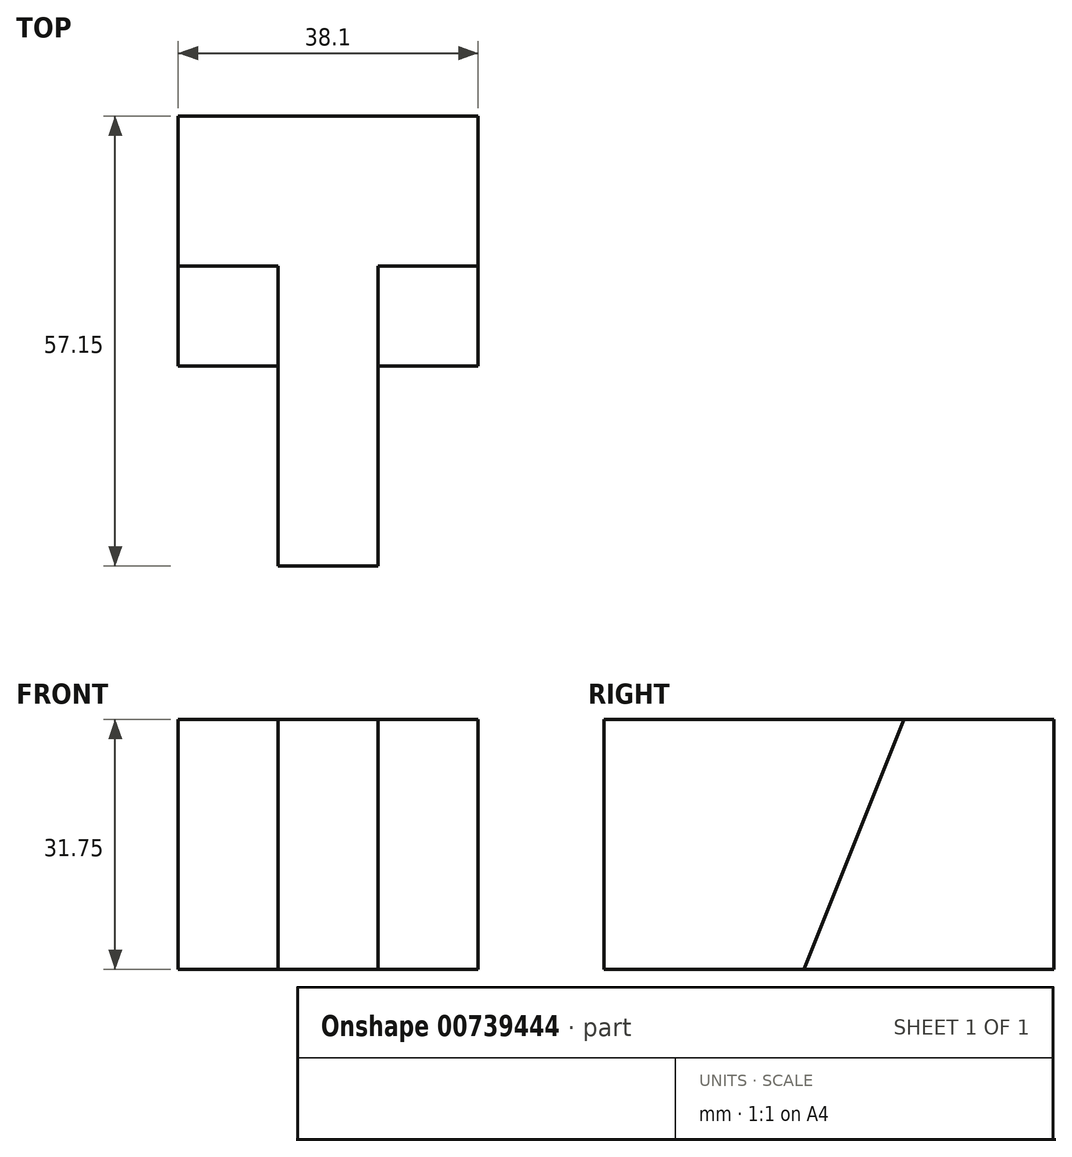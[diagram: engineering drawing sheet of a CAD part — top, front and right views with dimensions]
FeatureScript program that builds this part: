
annotation { "Feature Type Name" : "Feature", "Feature Type Description" : "" }
export const myFeature = defineFeature(function(context is Context, id is Id, definition is map)
    precondition{}
    {
        {
            var Q0;
            Q0=qCreatedBy(makeId("Top.planeOp"),FACE);
            var sketch = newSketch(context, id + "F0", { "sketchPlane" : qUnion([Q0])});
            skLineSegment(sketch, "E0", {"start": v(0, 0) * mm, "end": v(0, 25.4) * mm});
            skLineSegment(sketch, "E1", {"start": v(0, 25.4) * mm, "end": v(-12.7, 25.4) * mm});
            skLineSegment(sketch, "E2", {"start": v(-12.7, 25.4) * mm, "end": v(-12.7, 57.15) * mm});
            skLineSegment(sketch, "E3", {"start": v(-12.7, 57.15) * mm, "end": v(25.4, 57.15) * mm});
            skLineSegment(sketch, "E4", {"start": v(25.4, 57.15) * mm, "end": v(25.4, 25.4) * mm});
            skLineSegment(sketch, "E5", {"start": v(25.4, 25.4) * mm, "end": v(12.7, 25.4) * mm});
            skLineSegment(sketch, "E6", {"start": v(12.7, 25.4) * mm, "end": v(12.7, 0) * mm});
            skLineSegment(sketch, "E7", {"start": v(12.7, 0) * mm, "end": v(0, 0) * mm});
            skSolve(sketch);
        }
        {
            var Q0;
            Q0=makeQuery(id+"F0.imprint","IMPRINT",FACE,{"disambiguationData":[TD([[makeQuery(id+"F0.imprint","IMPRINT",EDGE,{"derivedFrom":sQuery(id+"F0.wireOp",EDGE,"E0")}),-1.0]])]});
            extrude(context, id + "F1", {"entities" : qUnion([Q0]), "depth" : 31.75 * mm, "offsetDistance" : 25.4 * mm});
        }
        {
            var Q0;
            Q0=makeQuery(id+"F1.opExtrude","SWEPT_FACE",FACE,{"disambiguationData":[OSD([sQuery(id+"F0.wireOp",EDGE,"E2")])]});
            var sketch = newSketch(context, id + "F2", { "sketchPlane" : qUnion([Q0])});
            skLineSegment(sketch, "E8", {"start": v(-25.4, 0) * mm, "end": v(-38.1, 31.75) * mm});
            skLineSegment(sketch, "E9", {"start": v(-38.1, 31.75) * mm, "end": v(-25.4, 31.75) * mm});
            skLineSegment(sketch, "E10", {"start": v(-25.4, 31.75) * mm, "end": v(-25.4, 0) * mm});
            skSolve(sketch);
        }
        {
            var Q0;
            Q0=makeQuery(id+"F2.imprint","IMPRINT",FACE,{"disambiguationData":[TD([[makeQuery(id+"F2.imprint","IMPRINT",EDGE,{"derivedFrom":sQuery(id+"F2.wireOp",EDGE,"E8")}),-1.0]])]});
            extrude(context, id + "F3", {"entities" : qUnion([Q0]), "operationType" : NewBodyOperationType.REMOVE, "oppositeDirection" : true, "depth" : 12.7 * mm, "offsetDistance" : 25.4 * mm});
        }
        {
            var Q0;
            Q0=makeQuery(id+"F1.opExtrude","SWEPT_FACE",FACE,{"disambiguationData":[OSD([sQuery(id+"F0.wireOp",EDGE,"E4")])]});
            var sketch = newSketch(context, id + "F4", { "sketchPlane" : qUnion([Q0])});
            skLineSegment(sketch, "E11", {"start": v(38.1, 31.75) * mm, "end": v(25.4, 0) * mm});
            skLineSegment(sketch, "E12", {"start": v(25.4, 0) * mm, "end": v(25.4, 31.75) * mm});
            skLineSegment(sketch, "E13", {"start": v(25.4, 31.75) * mm, "end": v(38.1, 31.75) * mm});
            skSolve(sketch);
        }
        {
            var Q0;
            Q0=makeQuery(id+"F4.imprint","IMPRINT",FACE,{"disambiguationData":[TD([[makeQuery(id+"F4.imprint","IMPRINT",EDGE,{"derivedFrom":sQuery(id+"F4.wireOp",EDGE,"E11")}),-1.0]])]});
            extrude(context, id + "F5", {"entities" : qUnion([Q0]), "operationType" : NewBodyOperationType.REMOVE, "oppositeDirection" : true, "depth" : 12.7 * mm, "offsetDistance" : 25.4 * mm});
        }
    });
